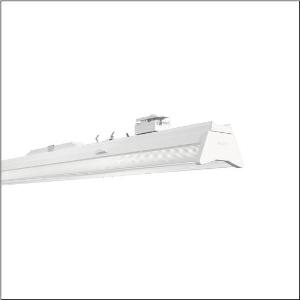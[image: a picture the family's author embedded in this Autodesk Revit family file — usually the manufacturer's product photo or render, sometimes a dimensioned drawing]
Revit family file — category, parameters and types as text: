
# Revit family: licross_r__11_performance_mo_51td16dn445g_6250
name_source: partatom
category: Lighting Fixtures
units: mm (PartAtom-declared; Revit-internal decimal feet)

## family parameters
Cut with Voids When Loaded = No
Host = Face
Light Source = No
Part Type = Normal
Room Calculation Point = No
Round Connector Dimension = Use Diameter
Shared = No

## types (1)
- --- (1 x LED, 4520 lm, 24.3 W, 4000K)
    Apparent Load = 24 VA
    CIE Flux Codes = 66 88 96 79 100
    Color Rendering = 80
    Color Temperature = 4000K
    Default Elevation = 1800 mm
    Description = Licross® 11 Performance MO, luminaire insert, of sheet steel, galvanised, coil coated, white, length: 1.500mm, width: 120mm, height: 123mm, LED rated luminous flux: 4.520lm, light colour: 840, control gear: DALI 2, with plug, 5-pole, with phase selection, mains connection: 220..240V, AC, 50/60Hz, rated input power: 24W, halogen-free wiring, primary light control with lens, of plastic, primary optical cover: cover, of PMMA, CAT 2 (L<= 3000cd/m²), light emission: direct/indirect distribution, primary light characteristic: symmetric, protection rating (complete): IP54, insulation class (complete): insulation class I (protective earthing), certification: CE, ENEC, VDE, UKCA, protection symbol: D if used in an environment with non-conductive dust loads with corresponding accessories, impact resistance: IK06, permissible ambient temperature for indoor applications: -25..+45°C, corresponds to IFS (International Featured Standards) requirements for safety and quality in the food industry, reducing of maximum allowable ambient temperature of 5°C with ceiling mounting, LABS conformity tested according to VDMA 24364:2018-05, packaging unit: 1 piece
    Height = 114 mm
    Lamp = 1 x LED
    Lamp Light Flux = 4520 lm
    Lamp Power = 24.3 W
    Lamp count = 1
    Length = 1500 mm
    Luminous efficacy = 186 lm/W
    Manufacturer = Siteco
    ModVariant = No
    Model = 51TD16DN445G
    Mounting Place = Ceiling
    Mounting Type = Pendant
    Number of Poles = 1
    OnlyDefault = Yes
    Power Factor = 1
    Product Name = Licross® 11 Performance MO
    Product group = luminaire insert
    ProductGroupID = 901
    Protection Class = Protection class I
    Protection Degree = IP 54
    RLX_Detail_Level = 1
    RLX_Emergency_Light_Flux = 0 lm
    RLX_Emergency_Type = 0
    RLX_Emergency_Type_DB = No
    RlxData = <blob elided: 33845 chars, md5=c09a6dcb>
    Socket = socket
    Standby Power = 0 W
    System Light Flux = 4520 lm
    System Power = 24 W
    Type Comments = factory setting: luminous flux: 100 % | dim-lin: 254 | 161 mA
    Type Image = l_1256138.jpg
    URL = http://relux.com
    VarID = @adj_022437
    Voltage = 0 V
    Weight = 0.00 kg
    Width = 120 mm

## geometry (parser evidence)
native form markers: Blend x4, Sweep x13
no freeform markers — native parametric forms only
